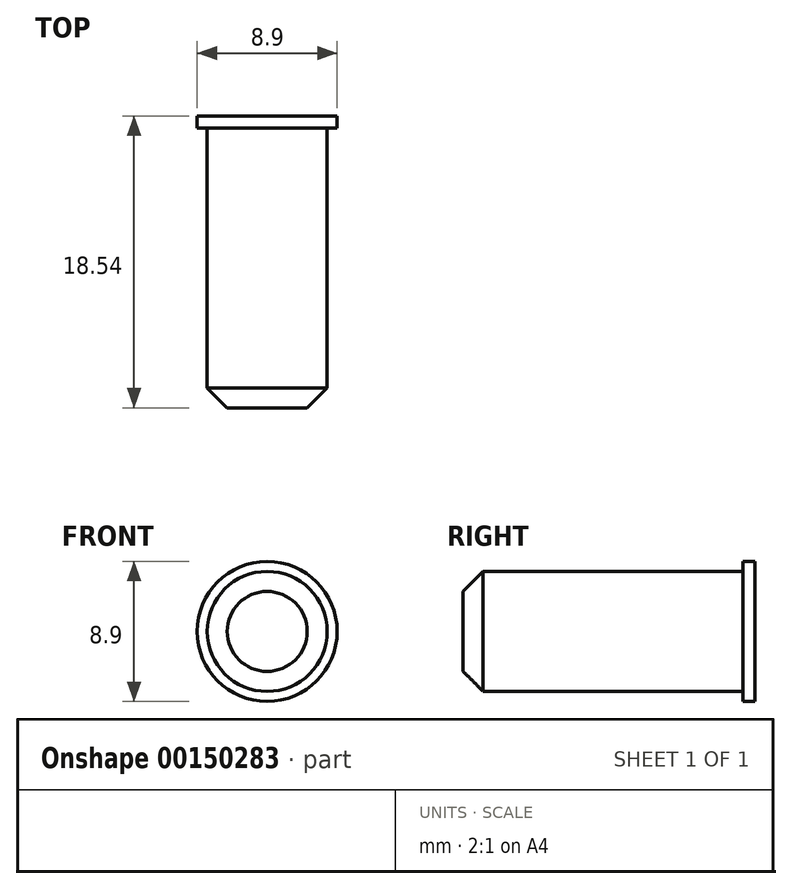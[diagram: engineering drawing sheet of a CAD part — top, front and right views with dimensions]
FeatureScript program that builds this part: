
annotation { "Feature Type Name" : "Feature", "Feature Type Description" : "" }
export const myFeature = defineFeature(function(context is Context, id is Id, definition is map)
    precondition{}
    {
        {
            var Q0;
            Q0=qCreatedBy(makeId("Front.planeOp"),FACE);
            var sketch = newSketch(context, id + "F0", { "sketchPlane" : qUnion([Q0])});
            skCircle(sketch, "E0", {"center": v(0, 0) * mm, "radius": 3.81 * mm});
            skSolve(sketch);
        }
        {
            var Q0;
            Q0 = qSketchRegion(id + "F0", true);
            extrude(context, id + "F1", {"entities" : qUnion([Q0]), "depth" : 17.78 * mm});
        }
        {
            var Q0;
            Q0=qCreatedBy(makeId("Front.planeOp"),FACE);
            var sketch = newSketch(context, id + "F2", { "sketchPlane" : qUnion([Q0])});
            skCircle(sketch, "E1", {"center": v(0, 0) * mm, "radius": 4.45 * mm});
            skSolve(sketch);
        }
        {
            var Q0;
            Q0=makeQuery(id+"F2.imprint","IMPRINT",FACE,{"disambiguationData":[TD([[makeQuery(id+"F2.imprint","IMPRINT",EDGE,{"derivedFrom":sQuery(id+"F2.wireOp",EDGE,"E1")}),1.0]])]});
            extrude(context, id + "F3", {"entities" : qUnion([Q0]), "operationType" : NewBodyOperationType.ADD, "oppositeDirection" : true, "depth" : 0.76 * mm});
        }
        {
            var Q0;
            Q0=makeQuery(id+"F1.opExtrude","CAP_EDGE",EDGE,{"disambiguationData":[OSD([sQuery(id+"F0.wireOp",EDGE,"E0")])],"isStart":false});
            chamfer(context, id + "F4", {"entities" : qUnion([Q0]), "width" : 1.27 * mm, "tangentPropagation" : true});
        }
    });
